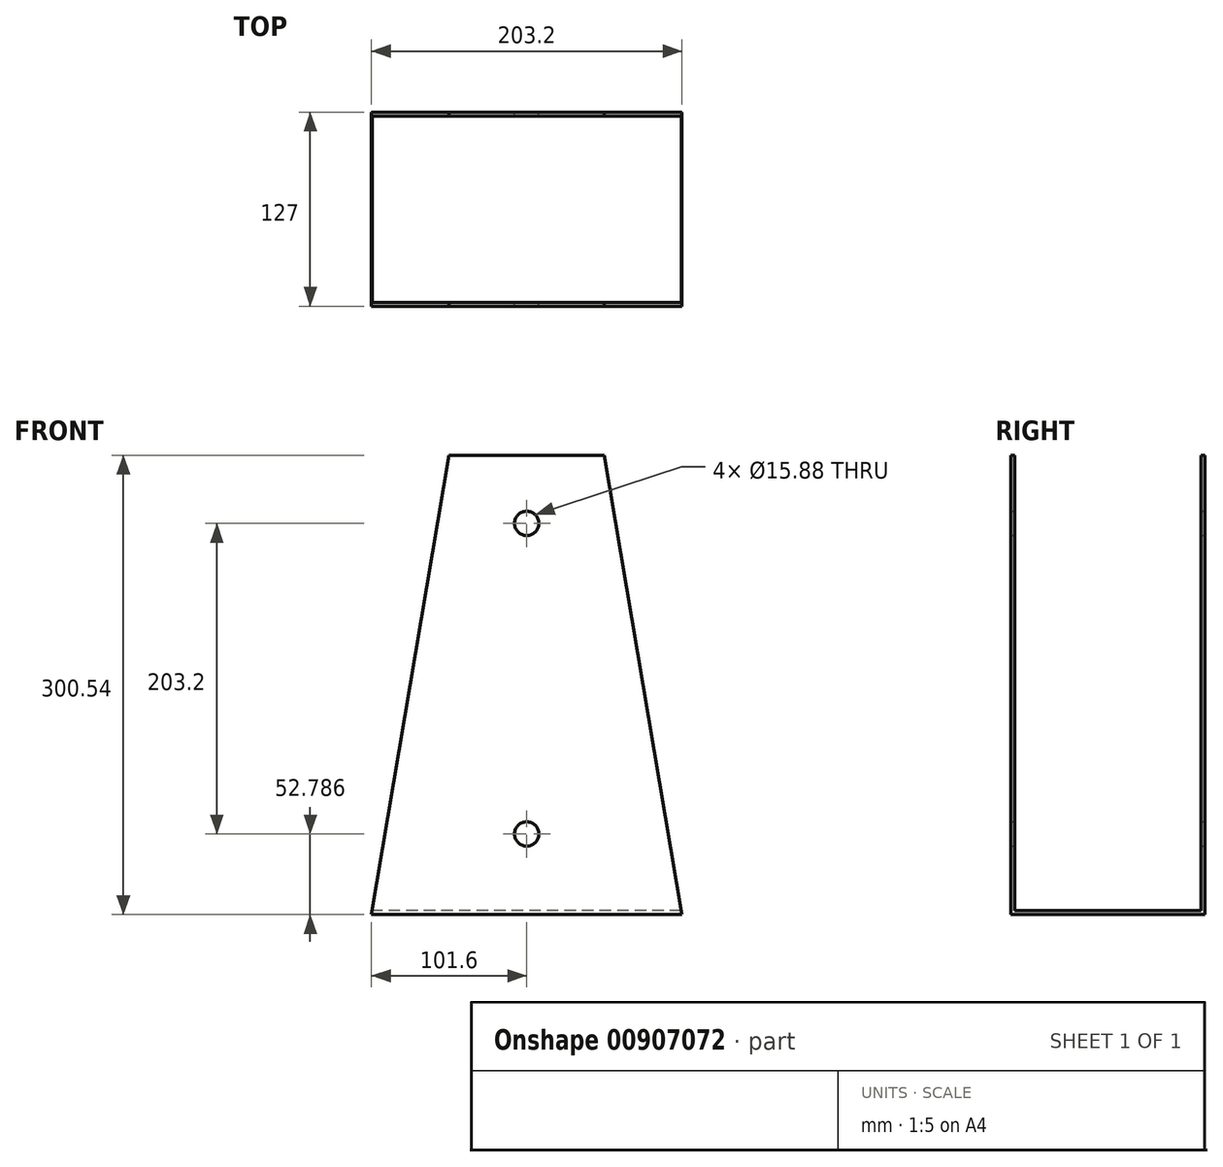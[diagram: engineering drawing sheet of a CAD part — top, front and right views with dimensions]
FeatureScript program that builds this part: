
annotation { "Feature Type Name" : "Feature", "Feature Type Description" : "" }
export const myFeature = defineFeature(function(context is Context, id is Id, definition is map)
    precondition{}
    {
        {
            var Q0;
            Q0=qCreatedBy(makeId("Front.planeOp"),FACE);
            var sketch = newSketch(context, id + "F0", { "sketchPlane" : qUnion([Q0])});
            skLineSegment(sketch, "E0", {"start": v(0, 0) * mm, "end": v(-101.6, 0) * mm});
            skLineSegment(sketch, "E1", {"start": v(0, 300.54) * mm, "end": v(-50.8, 300.54) * mm});
            skLineSegment(sketch, "E2", {"start": v(-50.8, 300.54) * mm, "end": v(-101.6, 0) * mm});
            skLineSegment(sketch, "E3.MirrorCS", {"start": v(0, 300.54) * mm, "end": v(50.8, 300.54) * mm});
            skLineSegment(sketch, "E4.MirrorCS", {"start": v(50.8, 300.54) * mm, "end": v(101.6, 0) * mm});
            skLineSegment(sketch, "E5.MirrorCS", {"start": v(0, 0) * mm, "end": v(101.6, 0) * mm});
            skCircle(sketch, "E6", {"center": v(0, 255.99) * mm, "radius": 7.94 * mm});
            skCircle(sketch, "E7", {"center": v(0, 52.79) * mm, "radius": 7.94 * mm});
            skSolve(sketch);
        }
        {
            var Q0;
            Q0=makeQuery(id+"F0.imprint","IMPRINT",FACE,{"disambiguationData":[TD([[makeQuery(id+"F0.imprint","IMPRINT",EDGE,{"derivedFrom":sQuery(id+"F0.wireOp",EDGE,"E0")}),-1.0]])]});
            extrude(context, id + "F1", {"entities" : qUnion([Q0]), "depth" : 127 * mm, "offsetDistance" : 25.4 * mm});
        }
        {
            var Q0;
            Q0=makeQuery(id+"F1.opExtrude","SWEPT_FACE",FACE,{"disambiguationData":[OSD([sQuery(id+"F0.wireOp",EDGE,"E2")])]});
            var Q1;
            Q1=makeQuery(id+"F1.opExtrude","SWEPT_FACE",FACE,{"disambiguationData":[OSD([sQuery(id+"F0.wireOp",EDGE,"E1"),sQuery(id+"F0.wireOp",EDGE,"E3.MirrorCS")])]});
            var Q2;
            Q2=makeQuery(id+"F1.opExtrude","SWEPT_FACE",FACE,{"disambiguationData":[OSD([sQuery(id+"F0.wireOp",EDGE,"E6")])]});
            var Q3;
            Q3=makeQuery(id+"F1.opExtrude","SWEPT_FACE",FACE,{"disambiguationData":[OSD([sQuery(id+"F0.wireOp",EDGE,"E7")])]});
            var Q4;
            Q4=makeQuery(id+"F1.opExtrude","SWEPT_FACE",FACE,{"disambiguationData":[OSD([sQuery(id+"F0.wireOp",EDGE,"E4.MirrorCS")])]});
            shell(context, id + "F2", {"entities" : qUnion([Q0, Q1, Q2, Q3, Q4]), "thickness" : 2.54 * mm});
        }
    });
